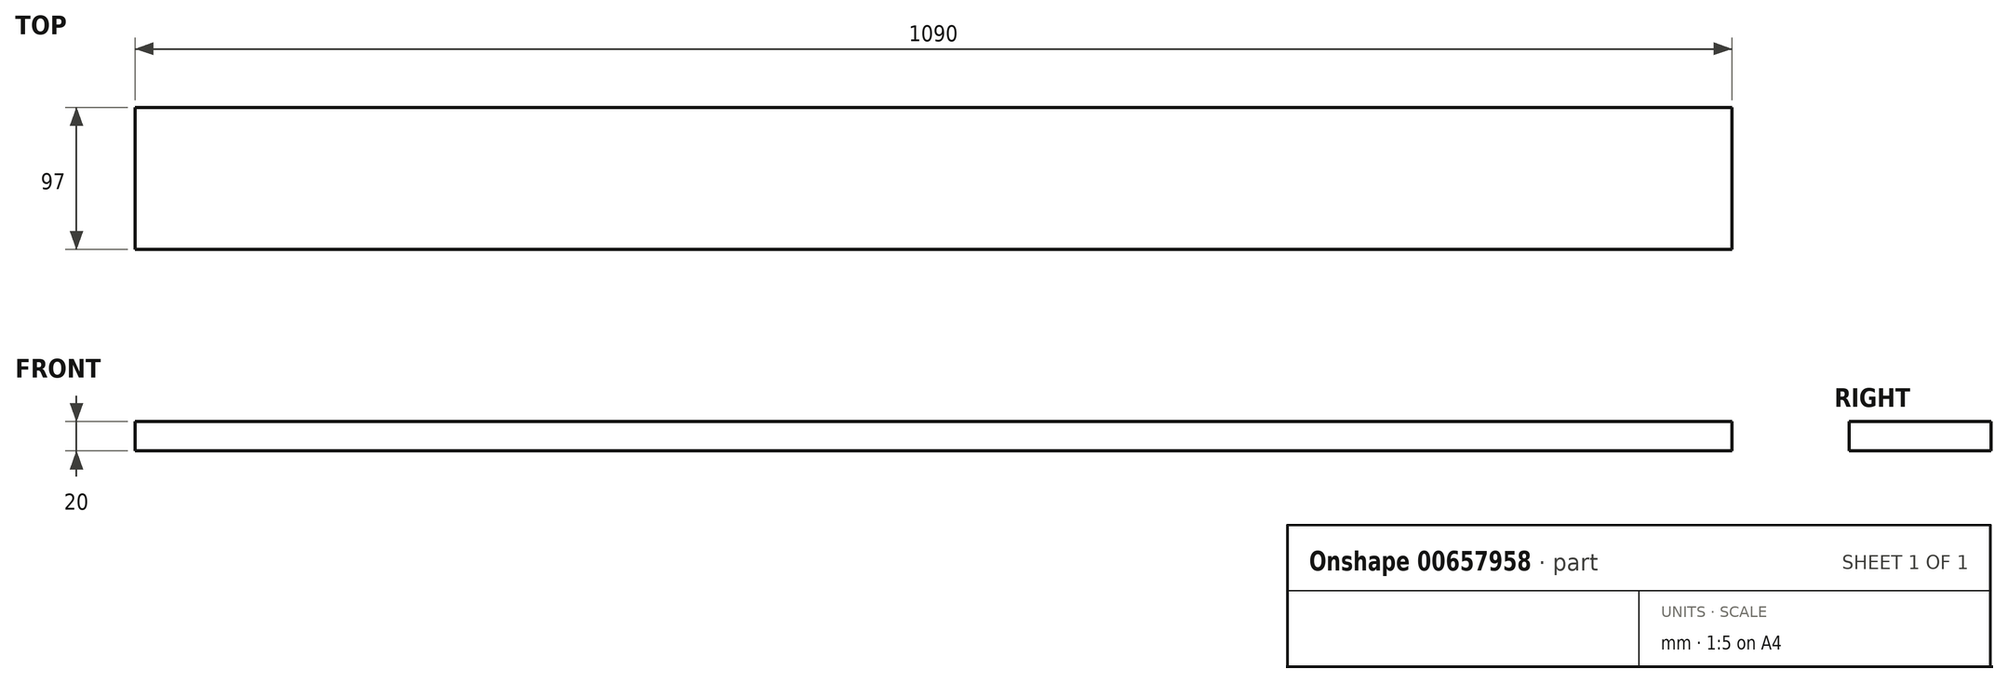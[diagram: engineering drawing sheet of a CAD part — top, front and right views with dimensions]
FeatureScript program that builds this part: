
annotation { "Feature Type Name" : "Feature", "Feature Type Description" : "" }
export const myFeature = defineFeature(function(context is Context, id is Id, definition is map)
    precondition{}
    {
        {
            var Q0;
            Q0=qCreatedBy(makeId("Right.planeOp"),FACE);
            var sketch = newSketch(context, id + "F0", { "sketchPlane" : qUnion([Q0])});
            skLineSegment(sketch, "E0.bottom", {"start": v(-48.5, 10) * mm, "end": v(48.5, 10) * mm});
            skLineSegment(sketch, "E0.top", {"start": v(-48.5, -10) * mm, "end": v(48.5, -10) * mm});
            skLineSegment(sketch, "E0.left", {"start": v(-48.5, 10) * mm, "end": v(-48.5, -10) * mm});
            skLineSegment(sketch, "E0.right", {"start": v(48.5, 10) * mm, "end": v(48.5, -10) * mm});
            skPoint(sketch, "E0.middle", {"position": v(0, 0) * mm});
            skSolve(sketch);
        }
        {
            var Q0;
            Q0 = qSketchRegion(id + "F0", true);
            extrude(context, id + "F1", {"entities" : qUnion([Q0]), "endBound" : BoundingType.SYMMETRIC, "depth" : 1090 * mm, "offsetDistance" : 25 * mm});
        }
    });
